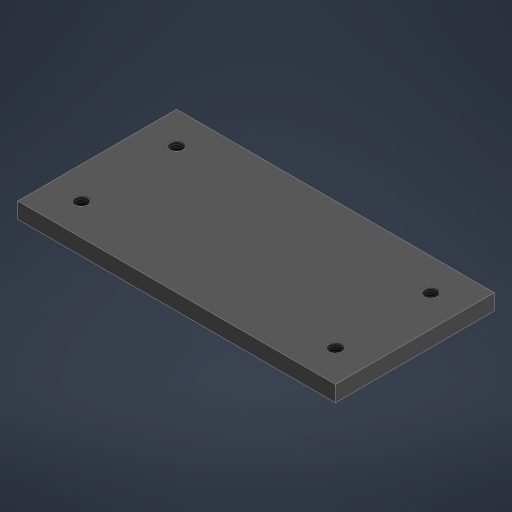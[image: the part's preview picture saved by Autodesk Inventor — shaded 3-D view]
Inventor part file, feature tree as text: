
AUTODESK INVENTOR PART (.ipt)
format: ipt  version: 2023 (Build 270158000, 158)  size: 176,128 bytes
history: native  units: mm
features: thread x4, sketch x2, extrude x1, hole x1
ambient origin geometry x8: Origin, YZ Plane, XZ Plane, XY Plane, X Axis, Y Axis, Z Axis, Center Point
bodies: Solid1 (feature_tree)
feature tree (8):
  extrude  "Extrusion1"  Depth=50.0mm
  hole  "Hole2"  [1 undecoded]
  thread  "Thread1"  [1 undecoded]
  thread  "Thread2"  [1 undecoded]
  thread  "Thread3"  [1 undecoded]
  thread  "Thread4"  [1 undecoded]
  sketch  "Sketch1"  dims[d0=100.0mm d1=50.0mm]
  sketch  "Sketch3"  dims[d2=5.0mm d3=0.0mm d13=80.0mm d14=30.0mm d15=4.0mm d16=6.0mm d17=4.0mm d18=2.0mm d19=90.0deg d20=6.0mm d21=0.0mm d22=5.0mm d23=0.0mm d24=5.0mm d25=0.0mm d26=5.0mm d27=0.0mm d28=5.0mm d29=0.0mm]
note: 5 required parameter values undecoded (feature->parameter linkage not recoverable at this tier; creation-order binding heuristic only, values carry confidence <= 0.55)
